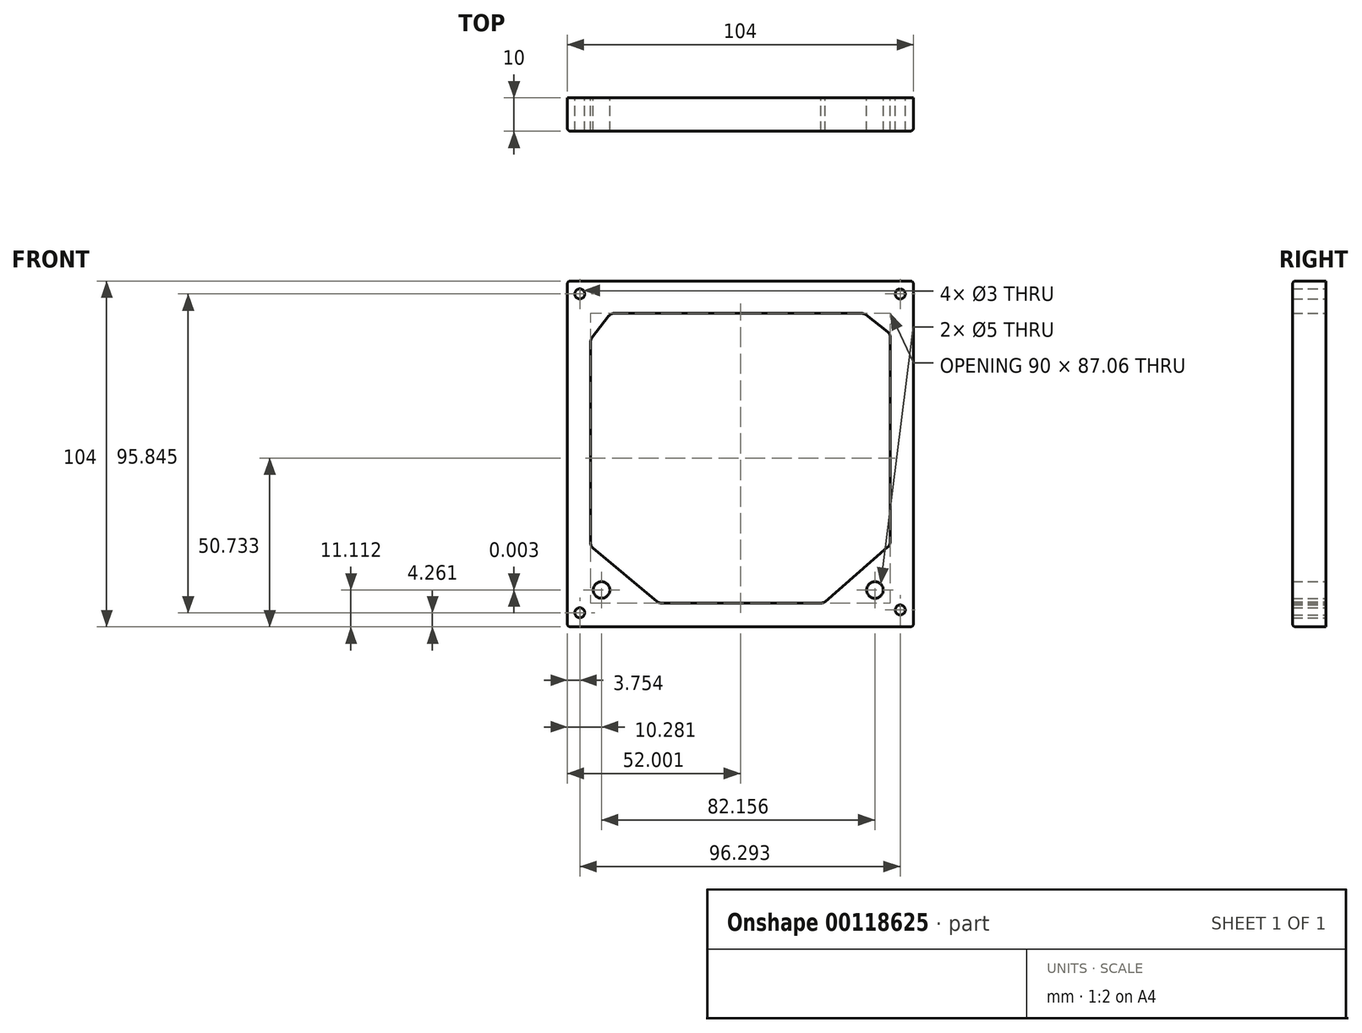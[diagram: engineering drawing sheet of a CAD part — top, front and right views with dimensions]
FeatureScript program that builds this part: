
annotation { "Feature Type Name" : "Feature", "Feature Type Description" : "" }
export const myFeature = defineFeature(function(context is Context, id is Id, definition is map)
    precondition{}
    {
        {
            var Q0;
            Q0=qCreatedBy(makeId("Front.planeOp"),FACE);
            var sketch = newSketch(context, id + "F0", { "sketchPlane" : qUnion([Q0])});
            skLineSegment(sketch, "E0.bottom", {"start": v(-50.98, 48.93) * mm, "end": v(53.02, 48.93) * mm});
            skLineSegment(sketch, "E0.top", {"start": v(-50.98, -55.07) * mm, "end": v(53.02, -55.07) * mm});
            skLineSegment(sketch, "E0.left", {"start": v(-50.98, 48.93) * mm, "end": v(-50.98, -55.07) * mm});
            skLineSegment(sketch, "E0.right", {"start": v(53.02, 48.93) * mm, "end": v(53.02, -55.07) * mm});
            skCircle(sketch, "E1", {"center": v(-47.23, 45.04) * mm, "radius": 1.5 * mm});
            skCircle(sketch, "E2", {"center": v(49.07, 45.02) * mm, "radius": 1.5 * mm});
            skCircle(sketch, "E3", {"center": v(-47.23, -50.8) * mm, "radius": 1.5 * mm});
            skCircle(sketch, "E4", {"center": v(49.07, -49.96) * mm, "radius": 1.5 * mm});
            skCircle(sketch, "E5", {"center": v(-40.7, -43.96) * mm, "radius": 2.5 * mm});
            skCircle(sketch, "E6", {"center": v(41.46, -43.96) * mm, "radius": 2.5 * mm});
            skSolve(sketch);
        }
        {
            var Q0;
            Q0=qCreatedBy(makeId("Front.planeOp"),FACE);
            var sketch = newSketch(context, id + "F1", { "sketchPlane" : qUnion([Q0])});
            skLineSegment(sketch, "E7", {"start": v(-36.9, 39.2) * mm, "end": v(37.43, 39.2) * mm});
            skLineSegment(sketch, "E8", {"start": v(46.02, 32.1) * mm, "end": v(46.02, -29.53) * mm});
            skLineSegment(sketch, "E9", {"start": v(45.34, -31.03) * mm, "end": v(26.5, -47.47) * mm});
            skLineSegment(sketch, "E10", {"start": v(25.23, -47.87) * mm, "end": v(-22.77, -47.87) * mm});
            skLineSegment(sketch, "E11", {"start": v(-24.05, -47.4) * mm, "end": v(-43.26, -31.4) * mm});
            skLineSegment(sketch, "E12", {"start": v(-43.98, -29.87) * mm, "end": v(-43.98, 30.58) * mm});
            skLineSegment(sketch, "E13", {"start": v(-43.57, 31.8) * mm, "end": v(-38.5, 38.41) * mm});
            skLineSegment(sketch, "E14", {"start": v(38.65, 38.78) * mm, "end": v(45.24, 33.68) * mm});
            skPoint(sketch, "E15.visualSharp", {"position": v(-43.98, -30.8) * mm});
            skArc(sketch, "E15.filletArc", {"start": v(-43.98, -29.87) * mm, "mid": v(-43.8, -30.72) * mm, "end": v(-43.26, -31.4) * mm});
            skPoint(sketch, "E16.visualSharp", {"position": v(-23.5, -47.87) * mm});
            skArc(sketch, "E16.filletArc", {"start": v(-24.05, -47.4) * mm, "mid": v(-23.45, -47.75) * mm, "end": v(-22.77, -47.87) * mm});
            skArc(sketch, "E17.filletArc", {"start": v(25.23, -47.87) * mm, "mid": v(25.9, -47.78) * mm, "end": v(26.5, -47.47) * mm});
            skArc(sketch, "E18.filletArc", {"start": v(45.34, -31.03) * mm, "mid": v(45.84, -30.35) * mm, "end": v(46.02, -29.53) * mm});
            skPoint(sketch, "E19.visualSharp", {"position": v(-43.98, 31.26) * mm});
            skArc(sketch, "E19.filletArc", {"start": v(-43.57, 31.8) * mm, "mid": v(-43.87, 31.23) * mm, "end": v(-43.98, 30.58) * mm});
            skPoint(sketch, "E20.visualSharp", {"position": v(-37.9, 39.2) * mm});
            skArc(sketch, "E20.filletArc", {"start": v(-36.9, 39.2) * mm, "mid": v(-37.79, 38.99) * mm, "end": v(-38.5, 38.41) * mm});
            skPoint(sketch, "E21.visualSharp", {"position": v(38.1, 39.2) * mm});
            skArc(sketch, "E21.filletArc", {"start": v(38.65, 38.78) * mm, "mid": v(38.07, 39.09) * mm, "end": v(37.43, 39.2) * mm});
            skPoint(sketch, "E22.visualSharp", {"position": v(46.02, 33.08) * mm});
            skArc(sketch, "E22.filletArc", {"start": v(46.02, 32.1) * mm, "mid": v(45.82, 32.98) * mm, "end": v(45.24, 33.68) * mm});
            skSolve(sketch);
        }
        {
            var Q0;
            Q0=makeQuery(id+"F0.imprint","IMPRINT",FACE,{"disambiguationData":[TD([[makeQuery(id+"F0.imprint","IMPRINT",EDGE,{"derivedFrom":sQuery(id+"F0.wireOp",EDGE,"E0.bottom")}),-1.0]])]});
            extrude(context, id + "F2", {"entities" : qUnion([Q0]), "depth" : 10 * mm});
        }
        {
            var Q0;
            Q0 = qSketchRegion(id + "F1", true);
            var Q1;
            Q1=makeQuery(id+"F2.opExtrude","CAP_FACE",FACE,{"disambiguationData":[OSD([sQuery(id+"F0.wireOp",EDGE,"E0.bottom"),sQuery(id+"F0.wireOp",EDGE,"E0.top"),sQuery(id+"F0.wireOp",EDGE,"E0.left"),sQuery(id+"F0.wireOp",EDGE,"E0.right"),sQuery(id+"F0.wireOp",EDGE,"E1"),sQuery(id+"F0.wireOp",EDGE,"E2"),sQuery(id+"F0.wireOp",EDGE,"E3"),sQuery(id+"F0.wireOp",EDGE,"E4")])],"isStart":false});
            extrude(context, id + "F3", {"entities" : qUnion([Q0, Q1]), "operationType" : NewBodyOperationType.REMOVE, "depth" : 25 * mm});
        }
        {
            var Q0;
            Q0=makeQuery(id+"F2.opExtrude","SWEPT_EDGE",EDGE,{"disambiguationData":[OSD([sQuery(id+"F0.wireOp",EDGE,"E0.bottom"),sQuery(id+"F0.wireOp",EDGE,"E0.left")])]});
            var Q1;
            Q1=makeQuery(id+"F2.opExtrude","CAP_EDGE",EDGE,{"disambiguationData":[OSD([sQuery(id+"F0.wireOp",EDGE,"E0.left")])],"isStart":false});
            var Q2;
            Q2=makeQuery(id+"F2.opExtrude","CAP_EDGE",EDGE,{"disambiguationData":[OSD([sQuery(id+"F0.wireOp",EDGE,"E0.bottom")])],"isStart":false});
            var Q3;
            Q3=makeQuery(id+"F2.opExtrude","SWEPT_EDGE",EDGE,{"disambiguationData":[OSD([sQuery(id+"F0.wireOp",EDGE,"E0.top"),sQuery(id+"F0.wireOp",EDGE,"E0.left")])]});
            var Q4;
            Q4=makeQuery(id+"F2.opExtrude","CAP_EDGE",EDGE,{"disambiguationData":[OSD([sQuery(id+"F0.wireOp",EDGE,"E0.top")])],"isStart":false});
            var Q5;
            Q5=makeQuery(id+"F2.opExtrude","CAP_EDGE",EDGE,{"disambiguationData":[OSD([sQuery(id+"F0.wireOp",EDGE,"E0.right")])],"isStart":false});
            var Q6;
            Q6=makeQuery(id+"F2.opExtrude","SWEPT_EDGE",EDGE,{"disambiguationData":[OSD([sQuery(id+"F0.wireOp",EDGE,"E0.bottom"),sQuery(id+"F0.wireOp",EDGE,"E0.right")])]});
            var Q7;
            Q7=makeQuery(id+"F2.opExtrude","SWEPT_EDGE",EDGE,{"disambiguationData":[OSD([sQuery(id+"F0.wireOp",EDGE,"E0.top"),sQuery(id+"F0.wireOp",EDGE,"E0.right")])]});
            fillet(context, id + "F4", {"entities" : qUnion([Q0, Q1, Q2, Q3, Q4, Q5, Q6, Q7]), "radius" : 1 * mm, "tangentPropagation" : true, "allowEdgeOverflow" : false});
        }
    });
